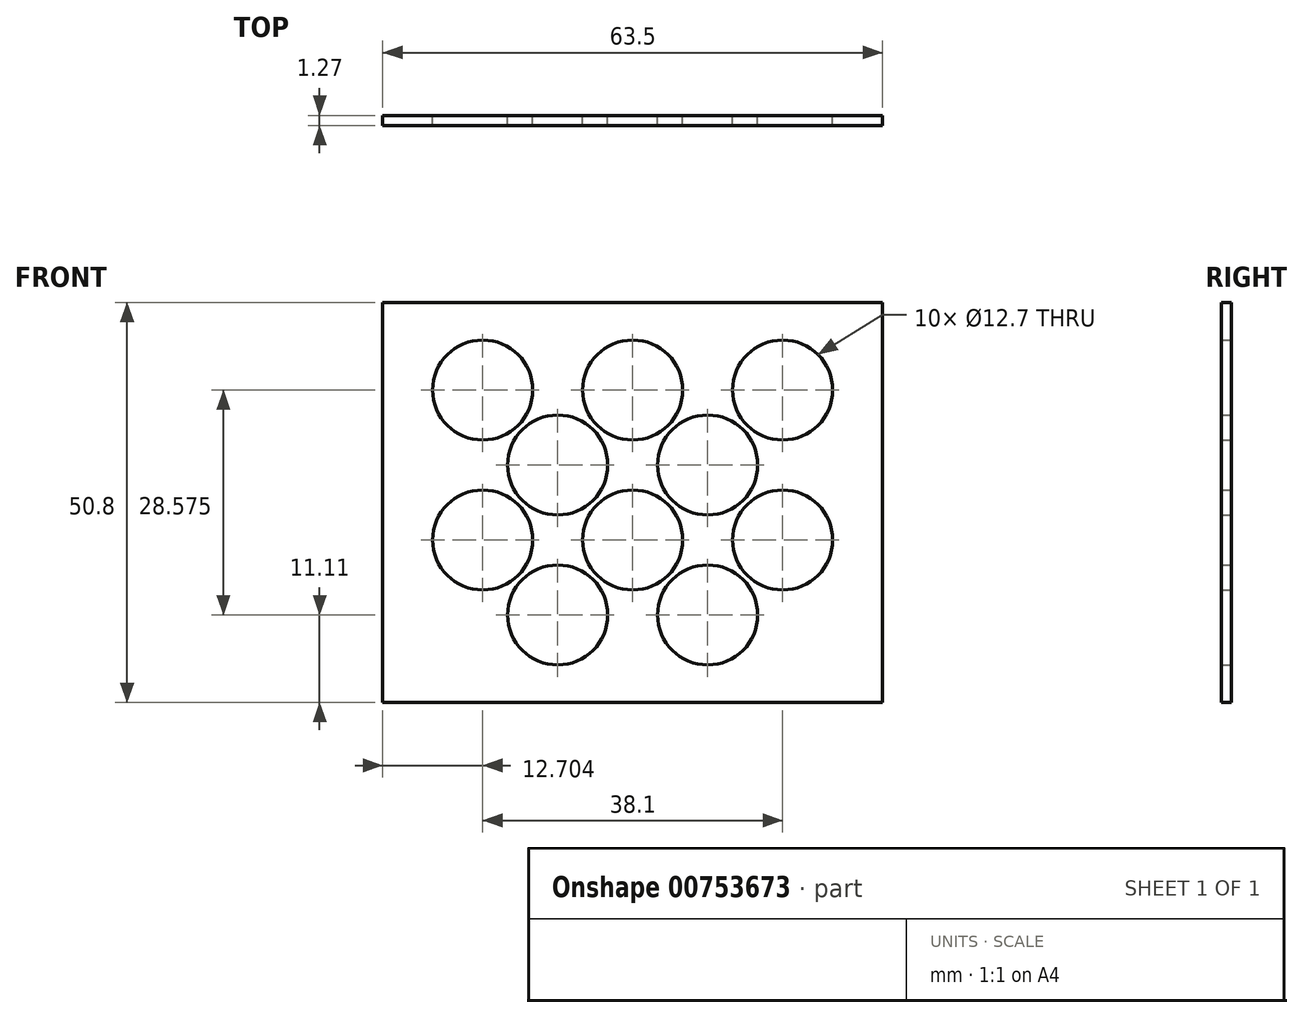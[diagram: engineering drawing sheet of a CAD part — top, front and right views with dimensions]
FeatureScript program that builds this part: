
annotation { "Feature Type Name" : "Feature", "Feature Type Description" : "" }
export const myFeature = defineFeature(function(context is Context, id is Id, definition is map)
    precondition{}
    {
        {
            var Q0;
            Q0=qCreatedBy(makeId("Front.planeOp"),FACE);
            var sketch = newSketch(context, id + "F0", { "sketchPlane" : qUnion([Q0])});
            skLineSegment(sketch, "E0.bottom", {"start": v(-30.1, 46.04) * mm, "end": v(33.4, 46.04) * mm});
            skLineSegment(sketch, "E0.top", {"start": v(-30.1, -4.76) * mm, "end": v(33.4, -4.76) * mm});
            skLineSegment(sketch, "E0.left", {"start": v(-30.1, 46.04) * mm, "end": v(-30.1, -4.76) * mm});
            skLineSegment(sketch, "E0.right", {"start": v(33.4, 46.04) * mm, "end": v(33.4, -4.76) * mm});
            skPoint(sketch, "E1", {"position": v(-17.4, 34.92) * mm});
            skPoint(sketch, "E2", {"position": v(1.65, 34.92) * mm});
            skPoint(sketch, "E3", {"position": v(20.7, 34.92) * mm});
            skPoint(sketch, "E4", {"position": v(-17.4, 15.88) * mm});
            skPoint(sketch, "E4.positionSnap0", {"position": v(1.65, 15.88) * mm});
            skPoint(sketch, "E5", {"position": v(20.7, 15.88) * mm});
            skPoint(sketch, "E6", {"position": v(-7.87, 25.4) * mm});
            skPoint(sketch, "E7", {"position": v(11.18, 25.4) * mm});
            skPoint(sketch, "E8", {"position": v(11.18, 6.35) * mm});
            skPoint(sketch, "E9", {"position": v(-7.87, 6.35) * mm});
            skCircle(sketch, "E10", {"center": v(-17.4, 34.92) * mm, "radius": 6.35 * mm});
            skCircle(sketch, "E11", {"center": v(-7.87, 25.4) * mm, "radius": 6.35 * mm});
            skCircle(sketch, "E12", {"center": v(1.65, 34.92) * mm, "radius": 6.35 * mm});
            skCircle(sketch, "E13", {"center": v(20.7, 34.92) * mm, "radius": 6.35 * mm});
            skCircle(sketch, "E14", {"center": v(11.18, 25.4) * mm, "radius": 6.35 * mm});
            skCircle(sketch, "E15", {"center": v(20.7, 15.88) * mm, "radius": 6.35 * mm});
            skCircle(sketch, "E16", {"center": v(11.18, 6.35) * mm, "radius": 6.35 * mm});
            skCircle(sketch, "E17", {"center": v(1.65, 15.88) * mm, "radius": 6.35 * mm});
            skCircle(sketch, "E18", {"center": v(-7.87, 6.35) * mm, "radius": 6.35 * mm});
            skCircle(sketch, "E19", {"center": v(-17.4, 15.88) * mm, "radius": 6.35 * mm});
            skSolve(sketch);
        }
        {
            var Q0;
            Q0=makeQuery(id+"F0.imprint","IMPRINT",FACE,{"disambiguationData":[TD([[makeQuery(id+"F0.imprint","IMPRINT",EDGE,{"derivedFrom":sQuery(id+"F0.wireOp",EDGE,"E0.bottom")}),-1.0]])]});
            extrude(context, id + "F1", {"entities" : qUnion([Q0]), "depth" : 1.27 * mm, "offsetDistance" : 25.4 * mm});
        }
    });
